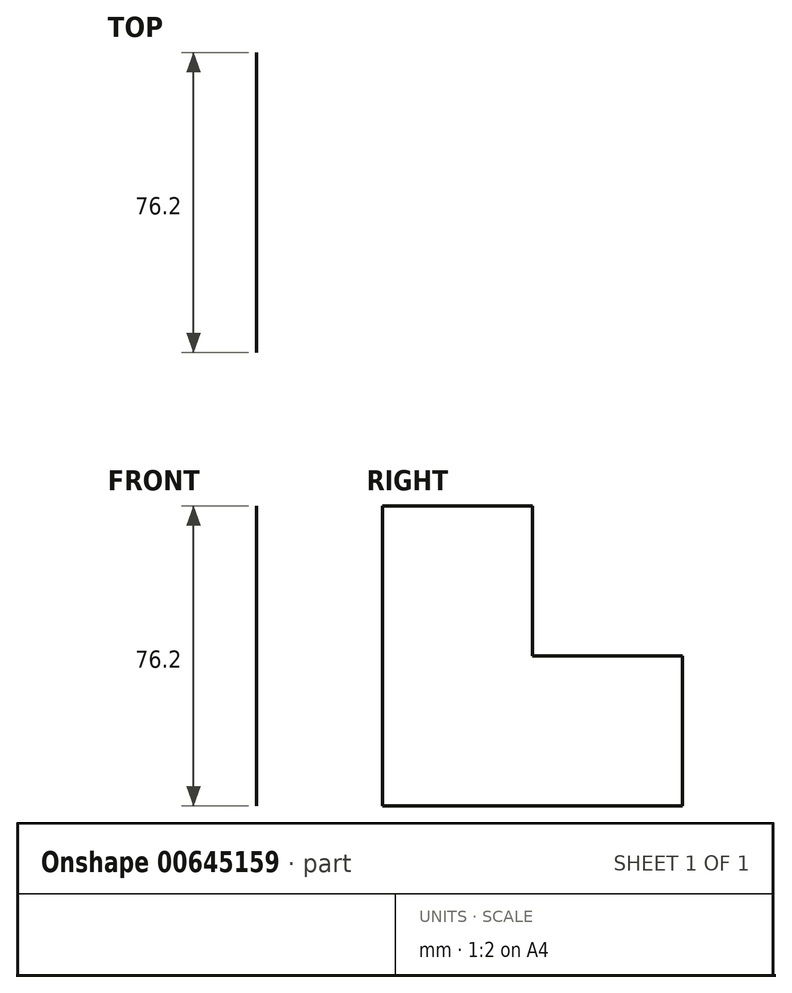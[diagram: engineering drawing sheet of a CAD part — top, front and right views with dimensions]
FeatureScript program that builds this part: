
annotation { "Feature Type Name" : "Feature", "Feature Type Description" : "" }
export const myFeature = defineFeature(function(context is Context, id is Id, definition is map)
    precondition{}
    {
        {
            var Q0;
            Q0=qCreatedBy(makeId("Right.planeOp"),FACE);
            var sketch = newSketch(context, id + "F0", { "sketchPlane" : qUnion([Q0])});
            skLineSegment(sketch, "E0.bottom", {"start": v(38.1, -38.1) * mm, "end": v(-38.1, -38.1) * mm});
            skLineSegment(sketch, "E0.top", {"start": v(38.1, 38.1) * mm, "end": v(-38.1, 38.1) * mm});
            skLineSegment(sketch, "E0.left", {"start": v(38.1, -38.1) * mm, "end": v(38.1, 38.1) * mm});
            skLineSegment(sketch, "E0.right", {"start": v(-38.1, -38.1) * mm, "end": v(-38.1, 38.1) * mm});
            skPoint(sketch, "E0.middle", {"position": v(0, 0) * mm});
            skSolve(sketch);
        }
        {
            var Q0;
            Q0=makeQuery(id+"F0.imprint","IMPRINT",FACE,{"disambiguationData":[TD([[makeQuery(id+"F0.imprint","IMPRINT",EDGE,{"derivedFrom":sQuery(id+"F0.wireOp",EDGE,"E0.bottom")}),-1.0]])]});
            extrude(context, id + "F1", {"entities" : qUnion([Q0]), "depth" : 1 / 406.4 * mm, "offsetDistance" : 25.4 * mm});
        }
        {
            var Q0;
            Q0=makeQuery(id+"F1.opExtrude","CAP_FACE",FACE,{"disambiguationData":[OSD([sQuery(id+"F0.wireOp",EDGE,"E0.bottom"),sQuery(id+"F0.wireOp",EDGE,"E0.top"),sQuery(id+"F0.wireOp",EDGE,"E0.left"),sQuery(id+"F0.wireOp",EDGE,"E0.right")])],"isStart":false});
            var sketch = newSketch(context, id + "F2", { "sketchPlane" : qUnion([Q0])});
            skLineSegment(sketch, "E1.bottom", {"start": v(0, 0) * mm, "end": v(38.1, 0) * mm});
            skLineSegment(sketch, "E1.top", {"start": v(0, 38.1) * mm, "end": v(38.1, 38.1) * mm});
            skLineSegment(sketch, "E1.left", {"start": v(0, 0) * mm, "end": v(0, 38.1) * mm});
            skLineSegment(sketch, "E1.right", {"start": v(38.1, 0) * mm, "end": v(38.1, 38.1) * mm});
            skSolve(sketch);
        }
        {
            var Q0;
            Q0=makeQuery(id+"F2.imprint","IMPRINT",FACE,{"disambiguationData":[TD([[makeQuery(id+"F2.imprint","IMPRINT",EDGE,{"derivedFrom":sQuery(id+"F2.wireOp",EDGE,"E1.bottom")}),1.0]])]});
            extrude(context, id + "F3", {"entities" : qUnion([Q0]), "operationType" : NewBodyOperationType.REMOVE, "oppositeDirection" : true, "depth" : 25.4 * mm, "offsetDistance" : 25.4 * mm});
        }
    });
